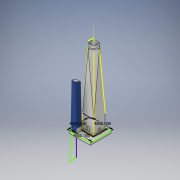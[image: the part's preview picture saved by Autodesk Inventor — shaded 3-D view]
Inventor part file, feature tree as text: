
AUTODESK INVENTOR PART (.ipt)
format: ipt  version: 2018 (Build 220112000, 112)  size: 401,408 bytes
history: native  units: in
note: dims shown in document units (in); Inventor stores cm internally (conversion verified against a paired STEP export)
features: sketch x45, plane x19, extrude x17, other x5, loft x5, fillet x2, projected_geometry x2, delete_face x1
ambient origin geometry x8: Origin, YZ Plane, XZ Plane, XY Plane, X Axis, Y Axis, Z Axis, Center Point
bodies: Solid1 (feature_tree)
feature tree (96):
  other  "Annotations"
  sketch  "Sketch1"  dims[d0=2580.0in d1=2580.0in]
  extrude  "Extrusion1"  Depth=2580.0in
  sketch  "3D Sketch1"
  sketch  "Sketch5"  dims[d31=13416.0in d32=13416.0in]
  sketch  "Sketch6"  dims[d33=90.0deg d34=13416.0in]
  plane  "Work Plane1"
  sketch  "Sketch7"  dims[d35=13416.0in d36=13416.0in]
  plane  "Work Plane2"
  plane  "Work Plane3"
  sketch  "Sketch8"  dims[d37=13416.0in d39=13416.0in]
  sketch  "Sketch9"  dims[d40=0.5805in d41=13416.0in]
  plane  "Work Plane4"
  sketch  "Sketch10"  dims[d42=0.6563in d43=0.0in d44=90.0deg]
  plane  "Work Plane5"
  loft  "Loft1"
  loft  "Loft2"
  extrude  "Extrusion5"  Depth=13416.0in
  sketch  "Sketch13"  dims[d49=0.0in d50=90.0deg d55=1.0in d56=0.0in]
  plane  "Work Plane6"
  extrude  "Extrusion6"  Depth=13416.0in
  plane  "Work Plane7"
  extrude  "Extrusion7"  Depth=13416.0in
  plane  "Work Plane8"
  plane  "Work Plane9"
  sketch  "Sketch16"  dims[d67=1500.0in d68=600.0in d69=0.0in]
  extrude  "Extrusion8"  Depth=13416.0in
  extrude  "Extrusion9"  TaperAngle=0.0deg  [1 undecoded]
  extrude  "Extrusion10"  TaperAngle=0.0deg  [1 undecoded]
  extrude  "Extrusion11"  Depth=1.0in TaperAngle=0.0deg
  delete_face  "Delete Face1"
  extrude  "Extrusion12"  Depth=1.0in TaperAngle=0.0deg
  sketch  "Sketch22"  dims[d88=200.0in d91=200.0in]
  sketch  "Sketch23"  dims[d92=0.0in d93=90.0deg d94=0.0in d95=90.0deg]
  sketch  "Sketch24"  dims[d96=669.0in d97=180.0deg d98=36.0in d99=0.0in]
  sketch  "Sketch25"  dims[d100=36.0in d101=0.0in d102=36.0in d103=0.0in d110=0.0in d111=90.0deg]
  sketch  "Sketch26"  dims[d112=0.0in d113=90.0deg d116=4800.0in]
  fillet  "Fillet1"  Radius=1.0in
  sketch  "Sketch27"  dims[d117=4800.0in d118=4800.0in]
  plane  "Work Plane11"
  loft  "Loft3"
  sketch  "Sketch29"  dims[d124=300.0in]
  extrude  "Extrusion14"  Depth=600.0in TaperAngle=0.0deg
  extrude  "Extrusion15"  Depth=400.0in
  sketch  "Sketch31"  dims[d126=1.0in d127=0.0in]
  extrude  "Extrusion16"  Depth=669.0in
  sketch  "Sketch32"  dims[d128=90.0deg]
  sketch  "Sketch33"  dims[d222=90.0deg]
  plane  "Work Plane12"
  sketch  "Sketch34"  dims[d223=200.0in d224=0.0in]
  loft  "Loft4"
  plane  "Work Plane13"
  sketch  "Sketch35"  dims[d225=200.0in d226=0.0in]
  extrude  "Extrusion19"  Depth=200.0in
  extrude  "Extrusion20"  TaperAngle=0.0deg  [1 undecoded]
  plane  "Work Plane14"
  sketch  "Sketch37"  dims[d228=90.0deg]
  sketch  "Sketch38"  dims[d237=1000.0in d238=0.0in]
  sketch  "Sketch39"  dims[d247=0.0in d248=90.0deg]
  sketch  "Sketch48"  dims[d249=0.0in d250=90.0deg]
  plane  "Work Plane15"
  sketch  "Sketch49"  dims[d114=0.2753in d115=21692.8722in]
  extrude  "Extrusion32"  Depth=36.0in TaperAngle=0.0deg
  extrude  "Extrusion33"  Depth=36.0in TaperAngle=0.0deg
  fillet  "Fillet2"  [1 undecoded]
  plane  "Work Plane16"
  sketch  "Sketch57"
  extrude  "Extrusion37"  Depth=4800.0in
  plane  "Work Plane19"
  sketch  "Sketch59"
  sketch  "Sketch60"
  plane  "Work Plane20"
  sketch  "Sketch61"
  plane  "Work Plane22"
  sketch  "Sketch65"
  plane  "Work Plane23"
  sketch  "Sketch66"
  loft  "Loft7"
  sketch  "Sketch2"  dims[d2=3000.0in d3=0.0in d30=90.0deg]
  sketch  "Sketch12"  dims[d45=0.0in d46=90.0deg d47=0.0in d48=90.0deg]
  sketch  "Sketch14"  dims[d57=1.0in d58=0.0in d59=1.0in d60=0.0in d61=1.0in d62=0.0in]
  sketch  "Sketch15"  dims[d63=1.0in d64=0.0in d65=120.0in d66=0.0in]
  sketch  "Sketch17"  dims[d71=400.0in d72=400.0in]
  sketch  "Sketch18"  dims[d73=1200.0in d74=0.0in d85=669.0in]
  other  "Srf1"
  sketch  "Sketch19"  dims[d86=669.0in d87=180.0deg]
  sketch  "Sketch28"  dims[d119=500.0in d120=0.0in]
  other  "Edges1"
  other  "Edges2"
  sketch  "Sketch36"  dims[d227=111.25in]
  sketch  "Sketch58"
  projected_geometry  "Projected Loop1"
  sketch  "Sketch67"
  sketch  "Sketch30"  dims[d125=300.0in]
  projected_geometry  "Project Cut Edges1"
  other  "Linear Dimension 2"
note: 4 required parameter values undecoded (feature->parameter linkage not recoverable at this tier; creation-order binding heuristic only, values carry confidence <= 0.55)
